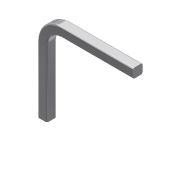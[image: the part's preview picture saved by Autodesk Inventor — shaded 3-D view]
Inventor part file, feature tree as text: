
AUTODESK INVENTOR PART (.ipt)
format: ipt  version: 2014 (Build 180170000, 170)  size: 111,616 bytes
history: native  units: in
note: dims shown in document units (in); Inventor stores cm internally (conversion verified against a paired STEP export)
features: extrude x1, fillet x1, sketch x1
ambient origin geometry x8: Origin, YZ Plane, XZ Plane, XY Plane, X Axis, Y Axis, Z Axis, Center Point
bodies: Solid1 (feature_tree)
feature tree (3):
  extrude  "Extrusion1"  Depth=0.03in
  fillet  "Fillet2"  Radius=0.045in
  sketch  "Sketch1"  dims[d0=0.3in d1=0.03in d2=0.045in d3=0.075in d4=0.095in d5=0.188in d6=0.03in d7=0.0in d9=0.005in]
